# Revit family: Bathroom_Faucet-Moen-Genta-1H_Lav-6702
name_source: partatom
category: Plumbing Fixtures
units: mm (PartAtom-declared; Revit-internal decimal feet)

## family parameters
Cut with Voids When Loaded = No
Host = Face
OmniClass Number = 23.45.55.17
OmniClass Title = Mixing Faucets
Part Type = Normal
Room Calculation Point = No
Round Connector Dimension = Use Radius
Shared = No

## types (1)
- 1H Lav - 6702
    Assembly Code = D2010900
    CW Connection = Yes
    CWFU = 0
    Cold Water Diameter = 0"
    Cold Water Radius = 0"
    Default Elevation = 4' - 0"
    Depth = 0' - 5 31/32"
    Description = Genta Chrome One-Handle Bathroom Faucet
    Domestic Water Flow Rate = 1.20 GPM
    Finish = Metal - Moen - Chrome
    Flow Rate = 1.20 GPM
    HW Connection = Yes
    HWFU = 0
    Hot Water Diameter = 0"
    Hot Water Radius = 0"
    Manufacturer = Moen
    Manufacturer Fax Number = (800) 848-6636
    Model = 6702
    Product Documentation Link = http://pro.moen.com
    Product Page URL = http://pro.moen.com
    Product data url = https://bimobject.com
    URL = http://pro.moen.com
    Vent Connection = Yes
    Version = 2014 - v1.0a
    WFU = 0
    Waste Connection = Yes
    Width = 0' - 5 7/8"

## geometry (parser evidence)
native form markers: Blend x4, Sweep x1
no freeform markers — native parametric forms only
